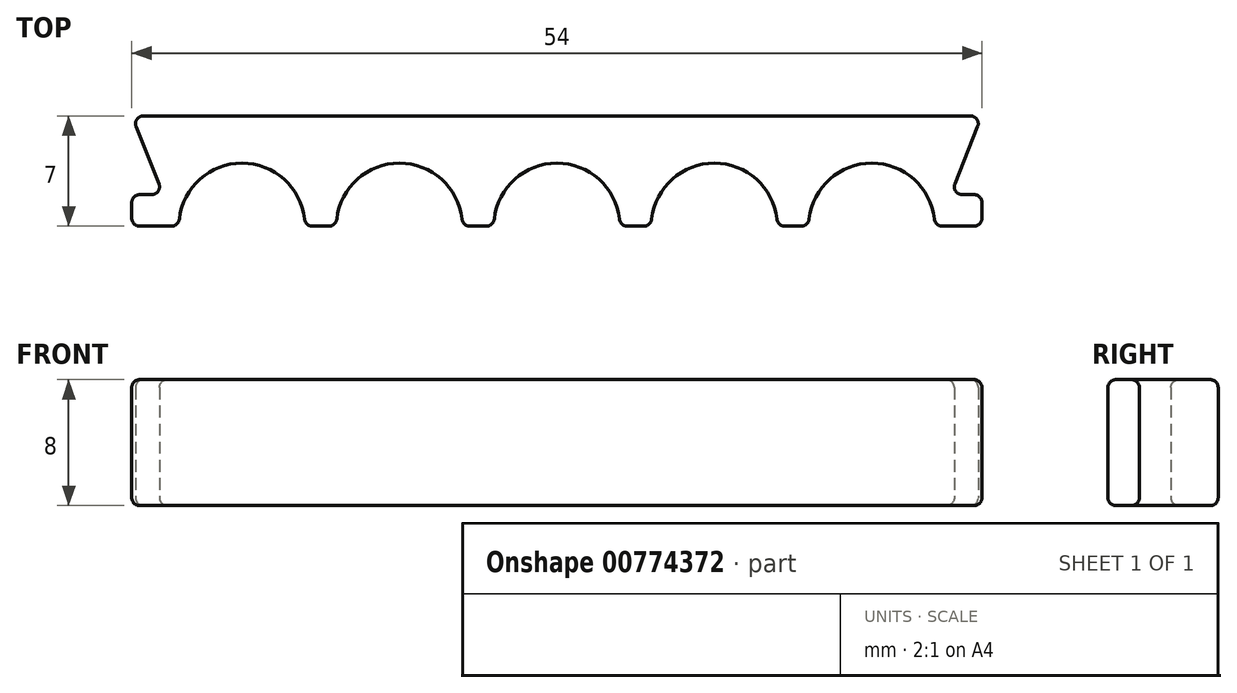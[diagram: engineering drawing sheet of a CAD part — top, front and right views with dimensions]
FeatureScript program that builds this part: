
annotation { "Feature Type Name" : "Feature", "Feature Type Description" : "" }
export const myFeature = defineFeature(function(context is Context, id is Id, definition is map)
    precondition{}
    {
        {
            var Q0;
            Q0=qCreatedBy(makeId("Top.planeOp"),FACE);
            var sketch = newSketch(context, id + "F0", { "sketchPlane" : qUnion([Q0])});
            skArc(sketch, "E0", {"start": v(3.98, 0.44) * mm, "mid": v(0, 4) * mm, "end": v(-3.98, 0.44) * mm});
            skArc(sketch, "E1", {"start": v(13.98, 0.44) * mm, "mid": v(10, 4) * mm, "end": v(6.02, 0.44) * mm});
            skArc(sketch, "E2", {"start": v(23.98, 0.44) * mm, "mid": v(20, 4) * mm, "end": v(16.02, 0.44) * mm});
            skArc(sketch, "E3", {"start": v(-6.02, 0.44) * mm, "mid": v(-10, 4) * mm, "end": v(-13.98, 0.44) * mm});
            skArc(sketch, "E4", {"start": v(-16.02, 0.44) * mm, "mid": v(-20, 4) * mm, "end": v(-23.98, 0.44) * mm});
            skLineSegment(sketch, "E5.bottom", {"start": v(-26.26, 7) * mm, "end": v(26.26, 7) * mm});
            skLineSegment(sketch, "E6", {"start": v(-26.5, 0) * mm, "end": v(-24.47, 0) * mm});
            skLineSegment(sketch, "E7.right", {"start": v(-27, 1.5) * mm, "end": v(-27, 0.5) * mm});
            skLineSegment(sketch, "E8.right", {"start": v(27, 1.5) * mm, "end": v(27, 0.5) * mm});
            skLineSegment(sketch, "E9", {"start": v(-26.73, 6.31) * mm, "end": v(-25.27, 2.69) * mm});
            skLineSegment(sketch, "E10", {"start": v(-25.74, 2) * mm, "end": v(-26.5, 2) * mm});
            skLineSegment(sketch, "E11", {"start": v(26.73, 6.31) * mm, "end": v(25.27, 2.69) * mm});
            skLineSegment(sketch, "E12", {"start": v(25.74, 2) * mm, "end": v(26.5, 2) * mm});
            skPoint(sketch, "E13.orphan", {"position": v(-31, -7) * mm});
            skPoint(sketch, "E14.orphan", {"position": v(-31, 7) * mm});
            skPoint(sketch, "E15.orphan", {"position": v(-31, 0) * mm});
            skLineSegment(sketch, "E16.trimOffspring", {"start": v(-15.53, 0) * mm, "end": v(-14.47, 0) * mm});
            skLineSegment(sketch, "E17.trimOffspring", {"start": v(-5.53, 0) * mm, "end": v(-4.47, 0) * mm});
            skLineSegment(sketch, "E18.trimOffspring", {"start": v(4.47, 0) * mm, "end": v(5.53, 0) * mm});
            skLineSegment(sketch, "E19.trimOffspring", {"start": v(14.47, 0) * mm, "end": v(15.53, 0) * mm});
            skLineSegment(sketch, "E20.trimOffspring", {"start": v(24.47, 0) * mm, "end": v(26.5, 0) * mm});
            skPoint(sketch, "E21.orphan", {"position": v(31, -7) * mm});
            skPoint(sketch, "E5.right.end.orphan", {"position": v(31, 0) * mm});
            skPoint(sketch, "E22.visualSharp", {"position": v(-25, 2) * mm});
            skArc(sketch, "E22.filletArc", {"start": v(-25.74, 2) * mm, "mid": v(-25.32, 2.22) * mm, "end": v(-25.27, 2.69) * mm});
            skPoint(sketch, "E23.visualSharp", {"position": v(25, 2) * mm});
            skArc(sketch, "E23.filletArc", {"start": v(25.27, 2.69) * mm, "mid": v(25.32, 2.22) * mm, "end": v(25.74, 2) * mm});
            skPoint(sketch, "E24.visualSharp", {"position": v(-27, 7) * mm});
            skArc(sketch, "E24.filletArc", {"start": v(-26.26, 7) * mm, "mid": v(-26.68, 6.78) * mm, "end": v(-26.73, 6.31) * mm});
            skPoint(sketch, "E25.newPointA", {"position": v(31, 7) * mm});
            skPoint(sketch, "E25.newPointB", {"position": v(27, 7) * mm});
            skArc(sketch, "E25.filletArc", {"start": v(26.73, 6.31) * mm, "mid": v(26.68, 6.78) * mm, "end": v(26.26, 7) * mm});
            skPoint(sketch, "E26.visualSharp", {"position": v(24, 0) * mm});
            skArc(sketch, "E26.filletArc", {"start": v(23.98, 0.44) * mm, "mid": v(24.14, 0.13) * mm, "end": v(24.47, 0) * mm});
            skPoint(sketch, "E27.visualSharp", {"position": v(16, 0) * mm});
            skArc(sketch, "E27.filletArc", {"start": v(15.53, 0) * mm, "mid": v(15.86, 0.13) * mm, "end": v(16.02, 0.44) * mm});
            skPoint(sketch, "E28.visualSharp", {"position": v(14, 0) * mm});
            skArc(sketch, "E28.filletArc", {"start": v(13.98, 0.44) * mm, "mid": v(14.14, 0.13) * mm, "end": v(14.47, 0) * mm});
            skPoint(sketch, "E29.visualSharp", {"position": v(6, 0) * mm});
            skArc(sketch, "E29.filletArc", {"start": v(5.53, 0) * mm, "mid": v(5.86, 0.13) * mm, "end": v(6.02, 0.44) * mm});
            skPoint(sketch, "E30.visualSharp", {"position": v(4, 0) * mm});
            skArc(sketch, "E30.filletArc", {"start": v(3.98, 0.44) * mm, "mid": v(4.14, 0.13) * mm, "end": v(4.47, 0) * mm});
            skPoint(sketch, "E31.visualSharp", {"position": v(-4, 0) * mm});
            skArc(sketch, "E31.filletArc", {"start": v(-4.47, 0) * mm, "mid": v(-4.14, 0.13) * mm, "end": v(-3.98, 0.44) * mm});
            skPoint(sketch, "E32.visualSharp", {"position": v(-6, 0) * mm});
            skArc(sketch, "E32.filletArc", {"start": v(-6.02, 0.44) * mm, "mid": v(-5.86, 0.13) * mm, "end": v(-5.53, 0) * mm});
            skPoint(sketch, "E33.visualSharp", {"position": v(-14, 0) * mm});
            skArc(sketch, "E33.filletArc", {"start": v(-14.47, 0) * mm, "mid": v(-14.14, 0.13) * mm, "end": v(-13.98, 0.44) * mm});
            skPoint(sketch, "E34.visualSharp", {"position": v(-16, 0) * mm});
            skArc(sketch, "E34.filletArc", {"start": v(-16.02, 0.44) * mm, "mid": v(-15.86, 0.13) * mm, "end": v(-15.53, 0) * mm});
            skPoint(sketch, "E35.visualSharp", {"position": v(-24, 0) * mm});
            skArc(sketch, "E35.filletArc", {"start": v(-24.47, 0) * mm, "mid": v(-24.14, 0.13) * mm, "end": v(-23.98, 0.44) * mm});
            skPoint(sketch, "E36.visualSharp", {"position": v(-27, 0) * mm});
            skArc(sketch, "E36.filletArc", {"start": v(-27, 0.5) * mm, "mid": v(-26.85, 0.15) * mm, "end": v(-26.5, 0) * mm});
            skPoint(sketch, "E37.visualSharp", {"position": v(-27, 2) * mm});
            skArc(sketch, "E37.filletArc", {"start": v(-26.5, 2) * mm, "mid": v(-26.85, 1.85) * mm, "end": v(-27, 1.5) * mm});
            skPoint(sketch, "E38.visualSharp", {"position": v(27, 2) * mm});
            skArc(sketch, "E38.filletArc", {"start": v(27, 1.5) * mm, "mid": v(26.85, 1.85) * mm, "end": v(26.5, 2) * mm});
            skPoint(sketch, "E39.visualSharp", {"position": v(27, 0) * mm});
            skArc(sketch, "E39.filletArc", {"start": v(26.5, 0) * mm, "mid": v(26.85, 0.15) * mm, "end": v(27, 0.5) * mm});
            skSolve(sketch);
        }
        {
            var Q0;
            Q0=makeQuery(id+"F0.imprint","IMPRINT",FACE,{"disambiguationData":[TD([[makeQuery(id+"F0.imprint","IMPRINT",EDGE,{"derivedFrom":sQuery(id+"F0.wireOp",EDGE,"E0")}),-1.0]])]});
            extrude(context, id + "F1", {"entities" : qUnion([Q0]), "depth" : 8 * mm, "offsetDistance" : 25 * mm});
        }
        {
            var Q0;
            Q0=makeQuery(id+"F1.opExtrude","CAP_FACE",FACE,{"disambiguationData":[OSD([sQuery(id+"F0.wireOp",EDGE,"E0"),sQuery(id+"F0.wireOp",EDGE,"E1"),sQuery(id+"F0.wireOp",EDGE,"E2"),sQuery(id+"F0.wireOp",EDGE,"E3"),sQuery(id+"F0.wireOp",EDGE,"E4"),sQuery(id+"F0.wireOp",EDGE,"E5.bottom"),sQuery(id+"F0.wireOp",EDGE,"E6"),sQuery(id+"F0.wireOp",EDGE,"E7.right"),sQuery(id+"F0.wireOp",EDGE,"E8.right"),sQuery(id+"F0.wireOp",EDGE,"E9"),sQuery(id+"F0.wireOp",EDGE,"E10"),sQuery(id+"F0.wireOp",EDGE,"E11"),sQuery(id+"F0.wireOp",EDGE,"E12"),sQuery(id+"F0.wireOp",EDGE,"E16.trimOffspring"),sQuery(id+"F0.wireOp",EDGE,"E17.trimOffspring"),sQuery(id+"F0.wireOp",EDGE,"E18.trimOffspring"),sQuery(id+"F0.wireOp",EDGE,"E19.trimOffspring"),sQuery(id+"F0.wireOp",EDGE,"E20.trimOffspring"),sQuery(id+"F0.wireOp",EDGE,"E22.filletArc"),sQuery(id+"F0.wireOp",EDGE,"E23.filletArc"),sQuery(id+"F0.wireOp",EDGE,"E24.filletArc"),sQuery(id+"F0.wireOp",EDGE,"E25.filletArc"),sQuery(id+"F0.wireOp",EDGE,"E26.filletArc"),sQuery(id+"F0.wireOp",EDGE,"E27.filletArc"),sQuery(id+"F0.wireOp",EDGE,"E28.filletArc"),sQuery(id+"F0.wireOp",EDGE,"E29.filletArc"),sQuery(id+"F0.wireOp",EDGE,"E30.filletArc"),sQuery(id+"F0.wireOp",EDGE,"E31.filletArc"),sQuery(id+"F0.wireOp",EDGE,"E32.filletArc"),sQuery(id+"F0.wireOp",EDGE,"E33.filletArc"),sQuery(id+"F0.wireOp",EDGE,"E34.filletArc"),sQuery(id+"F0.wireOp",EDGE,"E35.filletArc"),sQuery(id+"F0.wireOp",EDGE,"E36.filletArc"),sQuery(id+"F0.wireOp",EDGE,"E37.filletArc"),sQuery(id+"F0.wireOp",EDGE,"E38.filletArc"),sQuery(id+"F0.wireOp",EDGE,"E39.filletArc")])],"isStart":false});
            var Q1;
            Q1=makeQuery(id+"F1.opExtrude","CAP_FACE",FACE,{"disambiguationData":[OSD([sQuery(id+"F0.wireOp",EDGE,"E0"),sQuery(id+"F0.wireOp",EDGE,"E1"),sQuery(id+"F0.wireOp",EDGE,"E2"),sQuery(id+"F0.wireOp",EDGE,"E3"),sQuery(id+"F0.wireOp",EDGE,"E4"),sQuery(id+"F0.wireOp",EDGE,"E5.bottom"),sQuery(id+"F0.wireOp",EDGE,"E6"),sQuery(id+"F0.wireOp",EDGE,"E7.right"),sQuery(id+"F0.wireOp",EDGE,"E8.right"),sQuery(id+"F0.wireOp",EDGE,"E9"),sQuery(id+"F0.wireOp",EDGE,"E10"),sQuery(id+"F0.wireOp",EDGE,"E11"),sQuery(id+"F0.wireOp",EDGE,"E12"),sQuery(id+"F0.wireOp",EDGE,"E16.trimOffspring"),sQuery(id+"F0.wireOp",EDGE,"E17.trimOffspring"),sQuery(id+"F0.wireOp",EDGE,"E18.trimOffspring"),sQuery(id+"F0.wireOp",EDGE,"E19.trimOffspring"),sQuery(id+"F0.wireOp",EDGE,"E20.trimOffspring"),sQuery(id+"F0.wireOp",EDGE,"E22.filletArc"),sQuery(id+"F0.wireOp",EDGE,"E23.filletArc"),sQuery(id+"F0.wireOp",EDGE,"E24.filletArc"),sQuery(id+"F0.wireOp",EDGE,"E25.filletArc"),sQuery(id+"F0.wireOp",EDGE,"E26.filletArc"),sQuery(id+"F0.wireOp",EDGE,"E27.filletArc"),sQuery(id+"F0.wireOp",EDGE,"E28.filletArc"),sQuery(id+"F0.wireOp",EDGE,"E29.filletArc"),sQuery(id+"F0.wireOp",EDGE,"E30.filletArc"),sQuery(id+"F0.wireOp",EDGE,"E31.filletArc"),sQuery(id+"F0.wireOp",EDGE,"E32.filletArc"),sQuery(id+"F0.wireOp",EDGE,"E33.filletArc"),sQuery(id+"F0.wireOp",EDGE,"E34.filletArc"),sQuery(id+"F0.wireOp",EDGE,"E35.filletArc"),sQuery(id+"F0.wireOp",EDGE,"E36.filletArc"),sQuery(id+"F0.wireOp",EDGE,"E37.filletArc"),sQuery(id+"F0.wireOp",EDGE,"E38.filletArc"),sQuery(id+"F0.wireOp",EDGE,"E39.filletArc")])],"isStart":true});
            fillet(context, id + "F2", {"entities" : qUnion([Q0, Q1]), "radius" : .5 * mm, "tangentPropagation" : true, "allowEdgeOverflow" : false});
        }
    });
